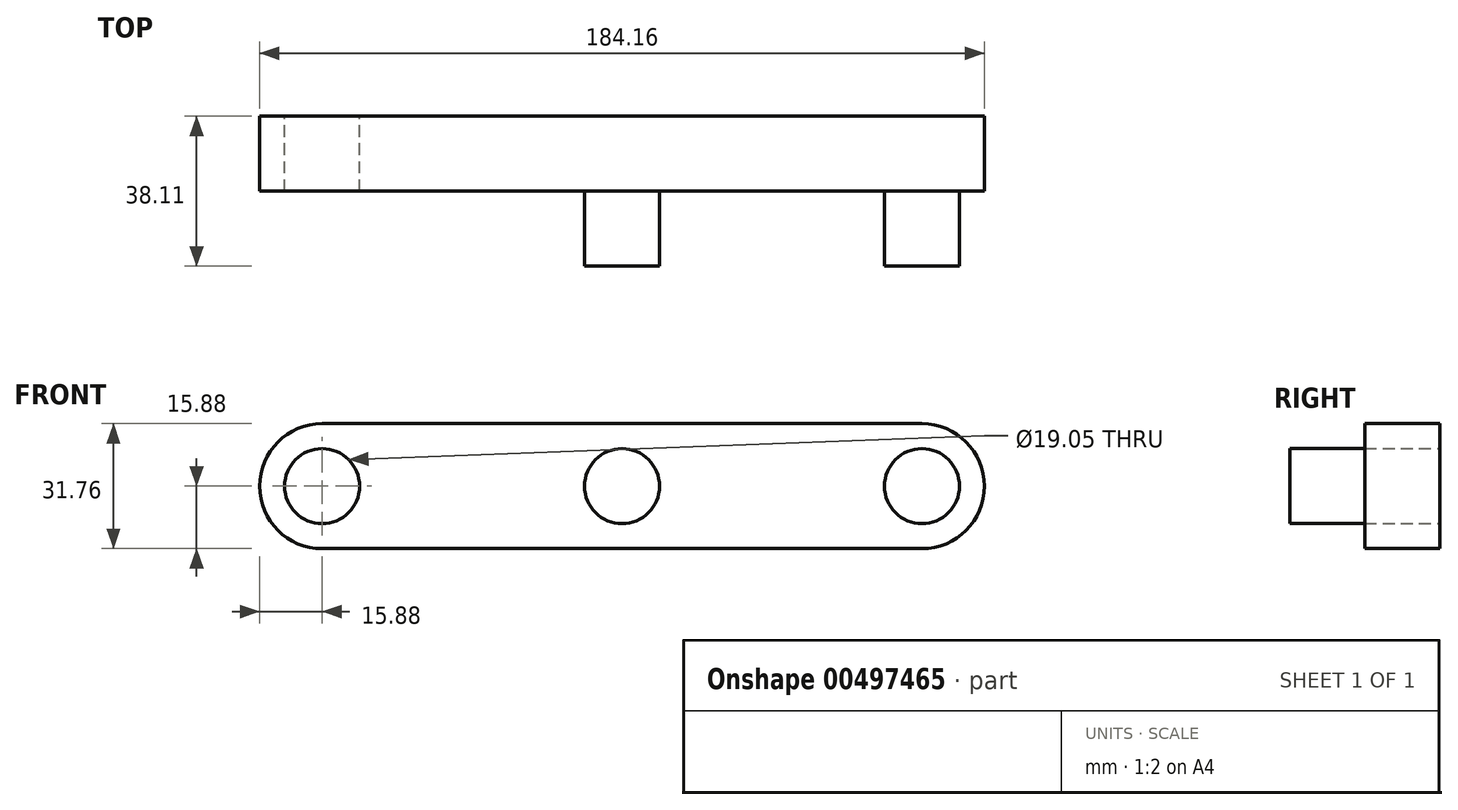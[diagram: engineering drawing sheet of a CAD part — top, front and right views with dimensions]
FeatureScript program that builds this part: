
annotation { "Feature Type Name" : "Feature", "Feature Type Description" : "" }
export const myFeature = defineFeature(function(context is Context, id is Id, definition is map)
    precondition{}
    {
        {
            var Q0;
            Q0=qCreatedBy(makeId("Front.planeOp"),FACE);
            var sketch = newSketch(context, id + "F0", { "sketchPlane" : qUnion([Q0])});
            skLineSegment(sketch, "E0.bottom", {"start": v(76.2, 15.88) * mm, "end": v(-76.2, 15.88) * mm});
            skLineSegment(sketch, "E0.top", {"start": v(76.2, -15.88) * mm, "end": v(-76.2, -15.88) * mm});
            skPoint(sketch, "E0.middle", {"position": v(0, 0) * mm});
            skCircle(sketch, "E1", {"center": v(-76.2, 0) * mm, "radius": 9.53 * mm});
            skCircle(sketch, "E2", {"center": v(76.2, 0) * mm, "radius": 9.53 * mm});
            skArc(sketch, "E3", {"start": v(-76.2, 15.88) * mm, "mid": v(-92.08, 0) * mm, "end": v(-76.2, -15.88) * mm});
            skArc(sketch, "E4", {"start": v(76.2, -15.88) * mm, "mid": v(92.08, 0) * mm, "end": v(76.2, 15.88) * mm});
            skPoint(sketch, "E0.right.start.orphan", {"position": v(-143.82, 15.87) * mm});
            skPoint(sketch, "E5.orphan", {"position": v(-143.82, -15.88) * mm});
            skPoint(sketch, "E6.orphan", {"position": v(143.82, 15.88) * mm});
            skPoint(sketch, "E7.orphan", {"position": v(143.82, -15.88) * mm});
            skSolve(sketch);
        }
        {
            var Q0;
            Q0=makeQuery(id+"F0.imprint","IMPRINT",FACE,{"disambiguationData":[TD([[makeQuery(id+"F0.imprint","IMPRINT",EDGE,{"derivedFrom":sQuery(id+"F0.wireOp",EDGE,"E0.bottom")}),1.0]])]});
            extrude(context, id + "F1", {"entities" : qUnion([Q0]), "endBound" : BoundingType.SYMMETRIC, "depth" : 19.05 * mm});
        }
        {
            var Q0;
            Q0=makeQuery(id+"F1.opExtrude","CAP_FACE",FACE,{"disambiguationData":[OSD([sQuery(id+"F0.wireOp",EDGE,"E0.bottom"),sQuery(id+"F0.wireOp",EDGE,"E0.top"),sQuery(id+"F0.wireOp",EDGE,"E1"),sQuery(id+"F0.wireOp",EDGE,"E2"),sQuery(id+"F0.wireOp",EDGE,"E3"),sQuery(id+"F0.wireOp",EDGE,"E4")])],"isStart":false});
            var sketch = newSketch(context, id + "F2", { "sketchPlane" : qUnion([Q0])});
            skCircle(sketch, "E8", {"center": v(0, 0) * mm, "radius": 9.53 * mm});
            skSolve(sketch);
        }
        {
            var Q0;
            Q0=makeQuery(id+"F2.imprint","IMPRINT",FACE,{"disambiguationData":[TD([[makeQuery(id+"F2.imprint","IMPRINT",EDGE,{"derivedFrom":sQuery(id+"F2.wireOp",EDGE,"E8")}),1.0]])]});
            extrude(context, id + "F3", {"entities" : qUnion([Q0]), "operationType" : NewBodyOperationType.ADD, "depth" : 19.05 * mm});
        }
        {
            var Q0;
            Q0=makeQuery(id+"F1.opExtrude","CAP_FACE",FACE,{"disambiguationData":[OSD([sQuery(id+"F0.wireOp",EDGE,"E0.bottom"),sQuery(id+"F0.wireOp",EDGE,"E0.top"),sQuery(id+"F0.wireOp",EDGE,"E1"),sQuery(id+"F0.wireOp",EDGE,"E2"),sQuery(id+"F0.wireOp",EDGE,"E3"),sQuery(id+"F0.wireOp",EDGE,"E4")])],"isStart":true});
            var sketch = newSketch(context, id + "F4", { "sketchPlane" : qUnion([Q0])});
            skCircle(sketch, "E9", {"center": v(-76.2, 0) * mm, "radius": 9.53 * mm});
            skSolve(sketch);
        }
        {
            var Q0;
            Q0=makeQuery(id+"F4.imprint","IMPRINT",FACE,{"disambiguationData":[TD([[makeQuery(id+"F4.imprint","IMPRINT",EDGE,{"derivedFrom":sQuery(id+"F4.wireOp",EDGE,"E9")}),-1.0]])]});
            extrude(context, id + "F5", {"entities" : qUnion([Q0]), "operationType" : NewBodyOperationType.ADD, "oppositeDirection" : true, "depth" : 38.1 * mm});
        }
    });
